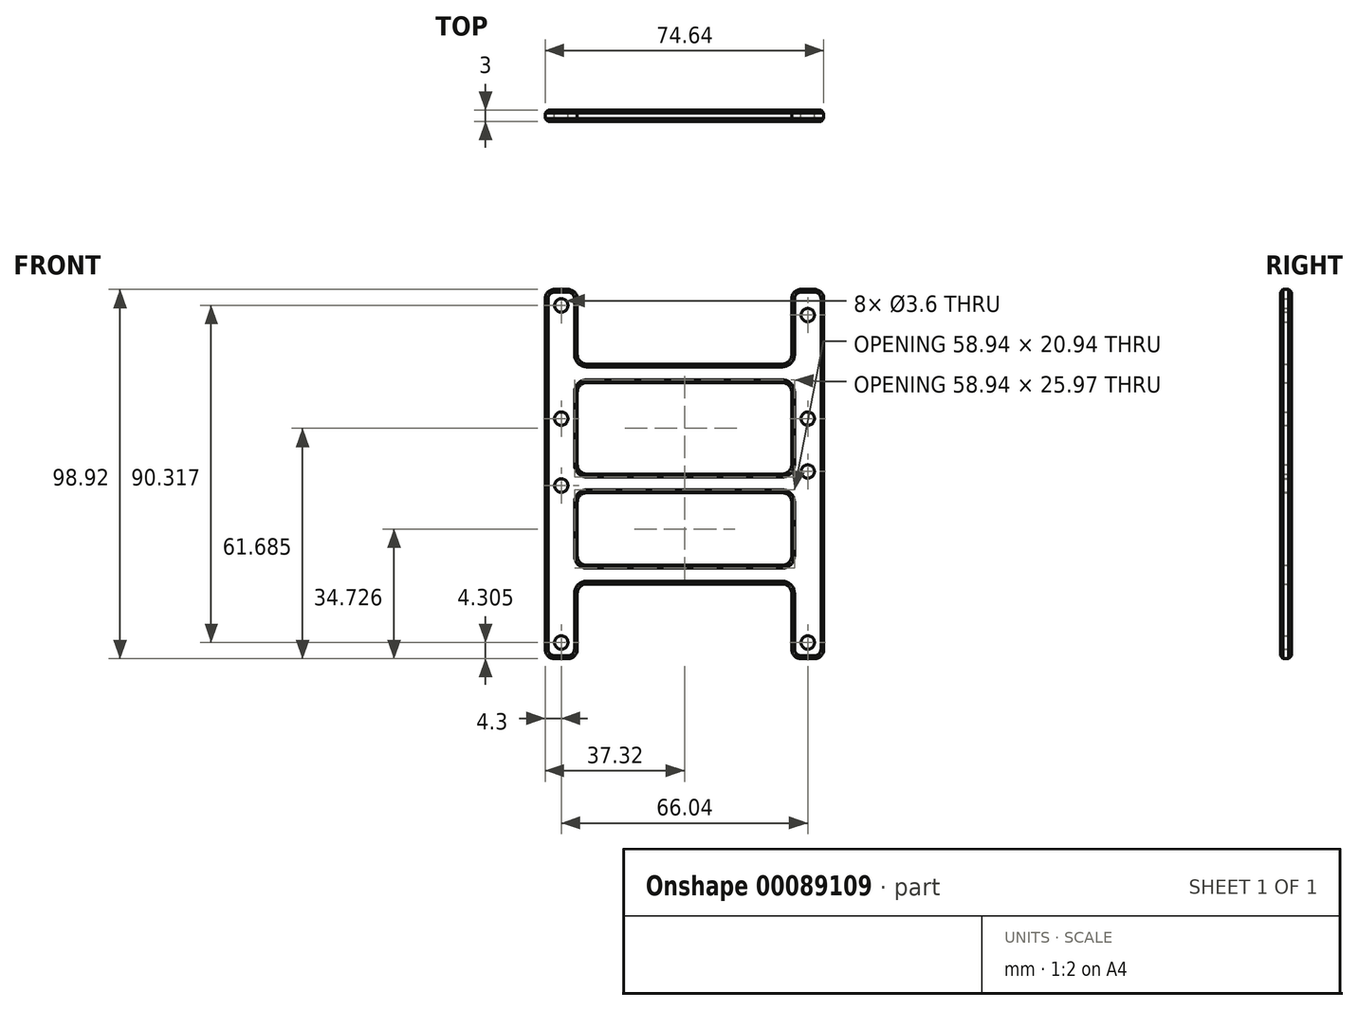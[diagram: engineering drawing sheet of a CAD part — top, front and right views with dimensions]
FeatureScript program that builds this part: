
annotation { "Feature Type Name" : "Feature", "Feature Type Description" : "" }
export const myFeature = defineFeature(function(context is Context, id is Id, definition is map)
    precondition{}
    {
        {
            var Q0;
            Q0=qCreatedBy(makeId("Front.planeOp"),FACE);
            var sketch = newSketch(context, id + "F0", { "sketchPlane" : qUnion([Q0])});
            skLineSegment(sketch, "E0.bottom", {"start": v(-37.32, 94.94) * mm, "end": v(-28.72, 94.94) * mm});
            skLineSegment(sketch, "E0.top", {"start": v(-37.32, -3.98) * mm, "end": v(-28.72, -3.98) * mm});
            skLineSegment(sketch, "E0.left", {"start": v(-37.32, 94.94) * mm, "end": v(-37.32, -3.98) * mm});
            skLineSegment(sketch, "E1", {"start": v(-33.02, 94.94) * mm, "end": v(-33.02, -55.68) * mm, "construction": true});
            skCircle(sketch, "E2", {"center": v(-33.02, 60.32) * mm, "radius": 1.8 * mm});
            skCircle(sketch, "E3", {"center": v(-33.02, 42.38) * mm, "radius": 1.8 * mm});
            skCircle(sketch, "E4", {"center": v(-33.02, 0.32) * mm, "radius": 1.8 * mm});
            skLineSegment(sketch, "E5", {"start": v(-28.72, 94.94) * mm, "end": v(-28.72, -3.98) * mm});
            skLineSegment(sketch, "E6.bottom", {"start": v(-28.72, 45.47) * mm, "end": v(0, 45.47) * mm});
            skLineSegment(sketch, "E6.top", {"start": v(-28.72, 40.47) * mm, "end": v(0, 40.47) * mm});
            skLineSegment(sketch, "E6.left", {"start": v(-28.72, 45.47) * mm, "end": v(-28.72, 40.47) * mm});
            skLineSegment(sketch, "E6.right", {"start": v(0, 45.47) * mm, "end": v(0, 40.47) * mm});
            skLineSegment(sketch, "E7.bottom", {"start": v(-28.75, 21.02) * mm, "end": v(0, 21.02) * mm});
            skLineSegment(sketch, "E7.top", {"start": v(-28.75, 16.02) * mm, "end": v(0, 16.02) * mm});
            skLineSegment(sketch, "E7.left", {"start": v(-28.75, 21.02) * mm, "end": v(-28.75, 16.02) * mm});
            skLineSegment(sketch, "E7.right", {"start": v(0, 21.02) * mm, "end": v(0, 16.02) * mm});
            skLineSegment(sketch, "E8.MirrorCS", {"start": v(28.75, 21.02) * mm, "end": v(28.75, 16.02) * mm});
            skCircle(sketch, "E9.MirrorC", {"center": v(33.02, 46.14) * mm, "radius": 1.8 * mm});
            skLineSegment(sketch, "E10.MirrorCS", {"start": v(28.72, 45.47) * mm, "end": v(28.72, 40.47) * mm});
            skLineSegment(sketch, "E11.MirrorCS", {"start": v(28.75, 16.02) * mm, "end": v(0, 16.02) * mm});
            skLineSegment(sketch, "E12.MirrorCS", {"start": v(28.75, 21.02) * mm, "end": v(0, 21.02) * mm});
            skCircle(sketch, "E13.MirrorC", {"center": v(33.02, 0.32) * mm, "radius": 1.8 * mm});
            skCircle(sketch, "E14.MirrorC", {"center": v(33.02, 60.32) * mm, "radius": 1.8 * mm});
            skLineSegment(sketch, "E15.MirrorCS", {"start": v(28.72, 40.47) * mm, "end": v(0, 40.47) * mm});
            skLineSegment(sketch, "E16.MirrorCS", {"start": v(37.32, 94.94) * mm, "end": v(37.32, -3.98) * mm});
            skLineSegment(sketch, "E17.MirrorCS", {"start": v(37.32, -3.98) * mm, "end": v(28.72, -3.98) * mm});
            skLineSegment(sketch, "E18.MirrorCS", {"start": v(28.72, 94.94) * mm, "end": v(28.72, -3.98) * mm});
            skLineSegment(sketch, "E19.MirrorCS", {"start": v(37.32, 94.94) * mm, "end": v(28.72, 94.94) * mm});
            skLineSegment(sketch, "E20.MirrorCS", {"start": v(28.72, 45.47) * mm, "end": v(0, 45.47) * mm});
            skCircle(sketch, "E21", {"center": v(-33.02, 90.64) * mm, "radius": 1.8 * mm});
            skLineSegment(sketch, "E22", {"start": v(33.02, -3.98) * mm, "end": v(33.02, 104.8) * mm, "construction": true});
            skCircle(sketch, "E23", {"center": v(33.02, 88.05) * mm, "radius": 1.8 * mm});
            skLineSegment(sketch, "E24", {"start": v(-28.72, 42.97) * mm, "end": v(-5.39, 46.14) * mm, "construction": true});
            skLineSegment(sketch, "E25", {"start": v(-28.72, 42.97) * mm, "end": v(-45.18, 40.73) * mm, "construction": true});
            skLineSegment(sketch, "E26", {"start": v(-28.72, 42.97) * mm, "end": v(43.34, 42.97) * mm, "construction": true});
            skLineSegment(sketch, "E27.bottom", {"start": v(-28.72, 74.94) * mm, "end": v(28.72, 74.94) * mm});
            skLineSegment(sketch, "E27.top", {"start": v(-28.72, 69.94) * mm, "end": v(28.72, 69.94) * mm});
            skLineSegment(sketch, "E27.left", {"start": v(-28.72, 74.94) * mm, "end": v(-28.72, 69.94) * mm});
            skLineSegment(sketch, "E27.right", {"start": v(28.72, 74.94) * mm, "end": v(28.72, 69.94) * mm});
            skSolve(sketch);
        }
        {
            var Q0;
            {var subQ5=sQuery(id+"F0.wireOp",EDGE,"E7.left");Q0=makeQuery(id+"F0.imprint","IMPRINT",FACE,{"disambiguationData":[TD([[makeQuery(id+"F0.imprint","IMPRINT",EDGE,{"derivedFrom":subQ5}),1.0]])]});}
            var Q1;
            {var subQ0=sQuery(id+"F0.wireOp",EDGE,"E8.MirrorCS");Q1=makeQuery(id+"F0.imprint","IMPRINT",FACE,{"disambiguationData":[TD([[makeQuery(id+"F0.imprint","IMPRINT",EDGE,{"derivedFrom":subQ0}),-1.0]])]});}
            var Q2;
            {var subQ5=sQuery(id+"F0.wireOp",EDGE,"E7.right");Q2=makeQuery(id+"F0.imprint","IMPRINT",FACE,{"disambiguationData":[TD([[makeQuery(id+"F0.imprint","IMPRINT",EDGE,{"derivedFrom":subQ5}),-1.0]])]});}
            var Q3;
            {var subQ0=sQuery(id+"F0.wireOp",EDGE,"E7.right");Q3=makeQuery(id+"F0.imprint","IMPRINT",FACE,{"disambiguationData":[TD([[makeQuery(id+"F0.imprint","IMPRINT",EDGE,{"derivedFrom":subQ0}),1.0]])]});}
            var Q4;
            {var subQ0=sQuery(id+"F0.wireOp",EDGE,"E15.MirrorCS");Q4=makeQuery(id+"F0.imprint","IMPRINT",FACE,{"disambiguationData":[TD([[makeQuery(id+"F0.imprint","IMPRINT",EDGE,{"derivedFrom":subQ0}),-1.0]])]});}
            var Q5;
            {var subQ9=sQuery(id+"F0.wireOp",EDGE,"E8.MirrorCS");Q5=makeQuery(id+"F0.imprint","IMPRINT",FACE,{"disambiguationData":[TD([[makeQuery(id+"F0.imprint","IMPRINT",EDGE,{"derivedFrom":subQ9}),1.0]])]});}
            var Q6;
            Q6=makeQuery(id+"F0.imprint","IMPRINT",FACE,{"disambiguationData":[TD([[makeQuery(id+"F0.imprint","IMPRINT",EDGE,{"derivedFrom":sQuery(id+"F0.wireOp",EDGE,"E6.bottom")}),-1.0]])]});
            var Q7;
            Q7=makeQuery(id+"F0.imprint","IMPRINT",FACE,{"disambiguationData":[TD([[makeQuery(id+"F0.imprint","IMPRINT",EDGE,{"derivedFrom":sQuery(id+"F0.wireOp",EDGE,"6060c022-7060-453b-8efb-dcd9e4211910.sketch_text.stroke-0")}),-1.0]])]});
            var Q8;
            Q8=makeQuery(id+"F0.imprint","IMPRINT",FACE,{"disambiguationData":[TD([[makeQuery(id+"F0.imprint","IMPRINT",EDGE,{"derivedFrom":sQuery(id+"F0.wireOp",EDGE,"6060c022-7060-453b-8efb-dcd9e4211910.sketch_text.stroke-80")}),-1.0]])]});
            var Q9;
            Q9=makeQuery(id+"F0.imprint","IMPRINT",FACE,{"disambiguationData":[TD([[makeQuery(id+"F0.imprint","IMPRINT",EDGE,{"derivedFrom":sQuery(id+"F0.wireOp",EDGE,"6060c022-7060-453b-8efb-dcd9e4211910.sketch_text.stroke-109")}),1.0]])]});
            var Q10;
            Q10=makeQuery(id+"F0.imprint","IMPRINT",FACE,{"disambiguationData":[TD([[makeQuery(id+"F0.imprint","IMPRINT",EDGE,{"derivedFrom":sQuery(id+"F0.wireOp",EDGE,"6060c022-7060-453b-8efb-dcd9e4211910.sketch_text.stroke-75")}),1.0]])]});
            var Q11;
            Q11=makeQuery(id+"F0.imprint","IMPRINT",FACE,{"disambiguationData":[TD([[makeQuery(id+"F0.imprint","IMPRINT",EDGE,{"derivedFrom":sQuery(id+"F0.wireOp",EDGE,"6060c022-7060-453b-8efb-dcd9e4211910.sketch_text.stroke-56")}),1.0]])]});
            var Q12;
            Q12=makeQuery(id+"F0.imprint","IMPRINT",FACE,{"disambiguationData":[TD([[makeQuery(id+"F0.imprint","IMPRINT",EDGE,{"derivedFrom":sQuery(id+"F0.wireOp",EDGE,"6060c022-7060-453b-8efb-dcd9e4211910.sketch_text.stroke-23")}),-1.0]])]});
            var Q13;
            Q13=makeQuery(id+"F0.imprint","IMPRINT",FACE,{"disambiguationData":[TD([[makeQuery(id+"F0.imprint","IMPRINT",EDGE,{"derivedFrom":sQuery(id+"F0.wireOp",EDGE,"6060c022-7060-453b-8efb-dcd9e4211910.sketch_text.stroke-13")}),-1.0]])]});
            var Q14;
            Q14=makeQuery(id+"F0.imprint","IMPRINT",FACE,{"disambiguationData":[TD([[makeQuery(id+"F0.imprint","IMPRINT",EDGE,{"derivedFrom":sQuery(id+"F0.wireOp",EDGE,"6060c022-7060-453b-8efb-dcd9e4211910.sketch_text.stroke-8")}),1.0]])]});
            var Q15;
            Q15=makeQuery(id+"F0.imprint","IMPRINT",FACE,{"disambiguationData":[TD([[makeQuery(id+"F0.imprint","IMPRINT",EDGE,{"derivedFrom":sQuery(id+"F0.wireOp",EDGE,"6060c022-7060-453b-8efb-dcd9e4211910.sketch_text.stroke-118")}),1.0]])]});
            var Q16;
            Q16=makeQuery(id+"F0.imprint","IMPRINT",FACE,{"disambiguationData":[TD([[makeQuery(id+"F0.imprint","IMPRINT",EDGE,{"derivedFrom":sQuery(id+"F0.wireOp",EDGE,"6060c022-7060-453b-8efb-dcd9e4211910.sketch_text.stroke-136")}),-1.0]])]});
            var Q17;
            Q17=makeQuery(id+"F0.imprint","IMPRINT",FACE,{"disambiguationData":[TD([[makeQuery(id+"F0.imprint","IMPRINT",EDGE,{"derivedFrom":sQuery(id+"F0.wireOp",EDGE,"6060c022-7060-453b-8efb-dcd9e4211910.sketch_text.stroke-124")}),-1.0]])]});
            var Q18;
            Q18=makeQuery(id+"F0.imprint","IMPRINT",FACE,{"disambiguationData":[TD([[makeQuery(id+"F0.imprint","IMPRINT",EDGE,{"derivedFrom":sQuery(id+"F0.wireOp",EDGE,"6060c022-7060-453b-8efb-dcd9e4211910.sketch_text.stroke-42")}),-1.0]])]});
            var Q19;
            Q19=makeQuery(id+"F0.imprint","IMPRINT",FACE,{"disambiguationData":[TD([[makeQuery(id+"F0.imprint","IMPRINT",EDGE,{"derivedFrom":sQuery(id+"F0.wireOp",EDGE,"6060c022-7060-453b-8efb-dcd9e4211910.sketch_text.stroke-187")}),-1.0]])]});
            var Q20;
            Q20=makeQuery(id+"F0.imprint","IMPRINT",FACE,{"disambiguationData":[TD([[makeQuery(id+"F0.imprint","IMPRINT",EDGE,{"derivedFrom":sQuery(id+"F0.wireOp",EDGE,"6060c022-7060-453b-8efb-dcd9e4211910.sketch_text.stroke-61")}),-1.0]])]});
            var Q21;
            {var subQ4=sQuery(id+"F0.wireOp",EDGE,"E0.bottom");Q21=makeQuery(id+"F0.imprint","IMPRINT",FACE,{"disambiguationData":[TD([[makeQuery(id+"F0.imprint","IMPRINT",EDGE,{"derivedFrom":subQ4}),-1.0]])]});}
            var Q22;
            Q22=makeQuery(id+"F0.imprint","IMPRINT",FACE,{"disambiguationData":[TD([[makeQuery(id+"F0.imprint","IMPRINT",EDGE,{"derivedFrom":sQuery(id+"F0.wireOp",EDGE,"6060c022-7060-453b-8efb-dcd9e4211910.sketch_text.stroke-195")}),-1.0]])]});
            var Q23;
            Q23=makeQuery(id+"F0.imprint","IMPRINT",FACE,{"disambiguationData":[TD([[makeQuery(id+"F0.imprint","IMPRINT",EDGE,{"derivedFrom":sQuery(id+"F0.wireOp",EDGE,"6060c022-7060-453b-8efb-dcd9e4211910.sketch_text.stroke-155")}),-1.0]])]});
            var Q24;
            Q24=makeQuery(id+"F0.imprint","IMPRINT",FACE,{"disambiguationData":[TD([[makeQuery(id+"F0.imprint","IMPRINT",EDGE,{"derivedFrom":sQuery(id+"F0.wireOp",EDGE,"6060c022-7060-453b-8efb-dcd9e4211910.sketch_text.stroke-234")}),-1.0]])]});
            var Q25;
            Q25=makeQuery(id+"F0.imprint","IMPRINT",FACE,{"disambiguationData":[TD([[makeQuery(id+"F0.imprint","IMPRINT",EDGE,{"derivedFrom":sQuery(id+"F0.wireOp",EDGE,"6060c022-7060-453b-8efb-dcd9e4211910.sketch_text.stroke-224")}),-1.0]])]});
            var Q26;
            Q26=makeQuery(id+"F0.imprint","IMPRINT",FACE,{"disambiguationData":[TD([[makeQuery(id+"F0.imprint","IMPRINT",EDGE,{"derivedFrom":sQuery(id+"F0.wireOp",EDGE,"6060c022-7060-453b-8efb-dcd9e4211910.sketch_text.stroke-212")}),-1.0]])]});
            var Q27;
            Q27=makeQuery(id+"F0.imprint","IMPRINT",FACE,{"disambiguationData":[TD([[makeQuery(id+"F0.imprint","IMPRINT",EDGE,{"derivedFrom":sQuery(id+"F0.wireOp",EDGE,"6060c022-7060-453b-8efb-dcd9e4211910.sketch_text.stroke-216")}),-1.0]])]});
            var Q28;
            Q28=makeQuery(id+"F0.imprint","IMPRINT",FACE,{"disambiguationData":[TD([[makeQuery(id+"F0.imprint","IMPRINT",EDGE,{"derivedFrom":sQuery(id+"F0.wireOp",EDGE,"6060c022-7060-453b-8efb-dcd9e4211910.sketch_text.stroke-183")}),-1.0]])]});
            var Q29;
            Q29=qSketchRegion(id+"F0",true);
            extrude(context, id + "F1", {"entities" : qUnion([Q0, Q1, Q2, Q3, Q4, Q5, Q6, Q7, Q8, Q9, Q10, Q11, Q12, Q13, Q14, Q15, Q16, Q17, Q18, Q19, Q20, Q21, Q22, Q23, Q24, Q25, Q26, Q27, Q28, Q29]), "depth" : 3 * mm});
        }
        {
            var Q0;
            Q0=makeQuery(id+"F1.opExtrude","SWEPT_EDGE",EDGE,{"disambiguationData":[OSD([sQuery(id+"F0.wireOp",EDGE,"E5"),sQuery(id+"F0.wireOp",EDGE,"E6.bottom"),sQuery(id+"F0.wireOp",EDGE,"E6.left")])]});
            var Q1;
            Q1=makeQuery(id+"F1.opExtrude","SWEPT_EDGE",EDGE,{"disambiguationData":[OSD([sQuery(id+"F0.wireOp",EDGE,"E18.MirrorCS"),sQuery(id+"F0.wireOp",EDGE,"E20.MirrorCS")])]});
            var Q2;
            Q2=makeQuery(id+"F1.opExtrude","SWEPT_EDGE",EDGE,{"disambiguationData":[OSD([sQuery(id+"F0.wireOp",EDGE,"E5"),sQuery(id+"F0.wireOp",EDGE,"E6.top"),sQuery(id+"F0.wireOp",EDGE,"E6.left")])]});
            var Q3;
            Q3=makeQuery(id+"F1.opExtrude","SWEPT_EDGE",EDGE,{"disambiguationData":[OSD([sQuery(id+"F0.wireOp",EDGE,"E15.MirrorCS"),sQuery(id+"F0.wireOp",EDGE,"E18.MirrorCS")])]});
            var Q4;
            Q4=makeQuery(id+"F1.opExtrude","SWEPT_EDGE",EDGE,{"disambiguationData":[OSD([sQuery(id+"F0.wireOp",EDGE,"E5"),sQuery(id+"F0.wireOp",EDGE,"E7.bottom")])]});
            var Q5;
            Q5=makeQuery(id+"F1.opExtrude","SWEPT_EDGE",EDGE,{"disambiguationData":[OSD([sQuery(id+"F0.wireOp",EDGE,"E12.MirrorCS"),sQuery(id+"F0.wireOp",EDGE,"E18.MirrorCS")])]});
            var Q6;
            Q6=makeQuery(id+"F1.opExtrude","SWEPT_EDGE",EDGE,{"disambiguationData":[OSD([sQuery(id+"F0.wireOp",EDGE,"E5"),sQuery(id+"F0.wireOp",EDGE,"E7.top")])]});
            var Q7;
            Q7=makeQuery(id+"F1.opExtrude","SWEPT_EDGE",EDGE,{"disambiguationData":[OSD([sQuery(id+"F0.wireOp",EDGE,"E11.MirrorCS"),sQuery(id+"F0.wireOp",EDGE,"E18.MirrorCS")])]});
            var Q8;
            Q8=makeQuery(id+"F1.opExtrude","SWEPT_EDGE",EDGE,{"disambiguationData":[OSD([sQuery(id+"F0.wireOp",EDGE,"E17.MirrorCS"),sQuery(id+"F0.wireOp",EDGE,"E18.MirrorCS")])]});
            var Q9;
            Q9=makeQuery(id+"F1.opExtrude","SWEPT_EDGE",EDGE,{"disambiguationData":[OSD([sQuery(id+"F0.wireOp",EDGE,"E16.MirrorCS"),sQuery(id+"F0.wireOp",EDGE,"E17.MirrorCS")])]});
            var Q10;
            Q10=makeQuery(id+"F1.opExtrude","SWEPT_EDGE",EDGE,{"disambiguationData":[OSD([sQuery(id+"F0.wireOp",EDGE,"E0.top"),sQuery(id+"F0.wireOp",EDGE,"E0.left")])]});
            var Q11;
            Q11=makeQuery(id+"F1.opExtrude","SWEPT_EDGE",EDGE,{"disambiguationData":[OSD([sQuery(id+"F0.wireOp",EDGE,"E0.top"),sQuery(id+"F0.wireOp",EDGE,"E5")])]});
            var Q12;
            Q12=makeQuery(id+"F1.opExtrude","SWEPT_EDGE",EDGE,{"disambiguationData":[OSD([sQuery(id+"F0.wireOp",EDGE,"E16.MirrorCS"),sQuery(id+"F0.wireOp",EDGE,"E19.MirrorCS")])]});
            var Q13;
            Q13=makeQuery(id+"F1.opExtrude","SWEPT_EDGE",EDGE,{"disambiguationData":[OSD([sQuery(id+"F0.wireOp",EDGE,"E18.MirrorCS"),sQuery(id+"F0.wireOp",EDGE,"E19.MirrorCS")])]});
            var Q14;
            Q14=makeQuery(id+"F1.opExtrude","SWEPT_EDGE",EDGE,{"disambiguationData":[OSD([sQuery(id+"F0.wireOp",EDGE,"E0.bottom"),sQuery(id+"F0.wireOp",EDGE,"E0.left")])]});
            var Q15;
            Q15=makeQuery(id+"F1.opExtrude","SWEPT_EDGE",EDGE,{"disambiguationData":[OSD([sQuery(id+"F0.wireOp",EDGE,"E0.bottom"),sQuery(id+"F0.wireOp",EDGE,"E5")])]});
            var Q16;
            Q16=makeQuery(id+"F1.opExtrude","SWEPT_EDGE",EDGE,{"disambiguationData":[OSD([sQuery(id+"F0.wireOp",EDGE,"E5"),sQuery(id+"F0.wireOp",EDGE,"E27.top"),sQuery(id+"F0.wireOp",EDGE,"E27.left")])]});
            var Q17;
            Q17=makeQuery(id+"F1.opExtrude","SWEPT_EDGE",EDGE,{"disambiguationData":[OSD([sQuery(id+"F0.wireOp",EDGE,"E18.MirrorCS"),sQuery(id+"F0.wireOp",EDGE,"E27.top"),sQuery(id+"F0.wireOp",EDGE,"E27.right")])]});
            var Q18;
            Q18=makeQuery(id+"F1.opExtrude","SWEPT_EDGE",EDGE,{"disambiguationData":[OSD([sQuery(id+"F0.wireOp",EDGE,"E5"),sQuery(id+"F0.wireOp",EDGE,"E27.bottom"),sQuery(id+"F0.wireOp",EDGE,"E27.left")])]});
            var Q19;
            Q19=makeQuery(id+"F1.opExtrude","SWEPT_EDGE",EDGE,{"disambiguationData":[OSD([sQuery(id+"F0.wireOp",EDGE,"E18.MirrorCS"),sQuery(id+"F0.wireOp",EDGE,"E27.bottom"),sQuery(id+"F0.wireOp",EDGE,"E27.right")])]});
            fillet(context, id + "F2", {"entities" : qUnion([Q0, Q1, Q2, Q3, Q4, Q5, Q6, Q7, Q8, Q9, Q10, Q11, Q12, Q13, Q14, Q15, Q16, Q17, Q18, Q19]), "radius" : 2.5 * mm, "tangentPropagation" : true, "allowEdgeOverflow" : false});
        }
        {
            var Q0;
            Q0=makeQuery(id+"F1.opExtrude","CAP_EDGE",EDGE,{"disambiguationData":[OSD([sQuery(id+"F0.wireOp",EDGE,"E7.top"),sQuery(id+"F0.wireOp",EDGE,"E11.MirrorCS")])],"isStart":true});
            var Q1;
            Q1=makeQuery(id+"F1.opExtrude","CAP_EDGE",EDGE,{"disambiguationData":[OSD([sQuery(id+"F0.wireOp",EDGE,"E6.top"),sQuery(id+"F0.wireOp",EDGE,"E15.MirrorCS")])],"isStart":true});
            var Q2;
            Q2=makeQuery(id+"F1.opExtrude","CAP_EDGE",EDGE,{"disambiguationData":[OSD([sQuery(id+"F0.wireOp",EDGE,"E0.bottom")])],"isStart":false});
            var Q3;
            Q3=makeQuery(id+"F1.opExtrude","CAP_EDGE",EDGE,{"disambiguationData":[OSD([sQuery(id+"F0.wireOp",EDGE,"E6.top"),sQuery(id+"F0.wireOp",EDGE,"E15.MirrorCS")])],"isStart":false});
            var Q4;
            Q4=makeQuery(id+"F1.opExtrude","CAP_EDGE",EDGE,{"disambiguationData":[OSD([sQuery(id+"F0.wireOp",EDGE,"E27.top")])],"isStart":false});
            var Q5;
            Q5=makeQuery(id+"F1.opExtrude","CAP_EDGE",EDGE,{"disambiguationData":[OSD([sQuery(id+"F0.wireOp",EDGE,"E27.top")])],"isStart":true});
            chamfer(context, id + "F3", {"entities" : qUnion([Q0, Q1, Q2, Q3, Q4, Q5]), "width" : .75 * mm, "tangentPropagation" : true});
        }
    });
